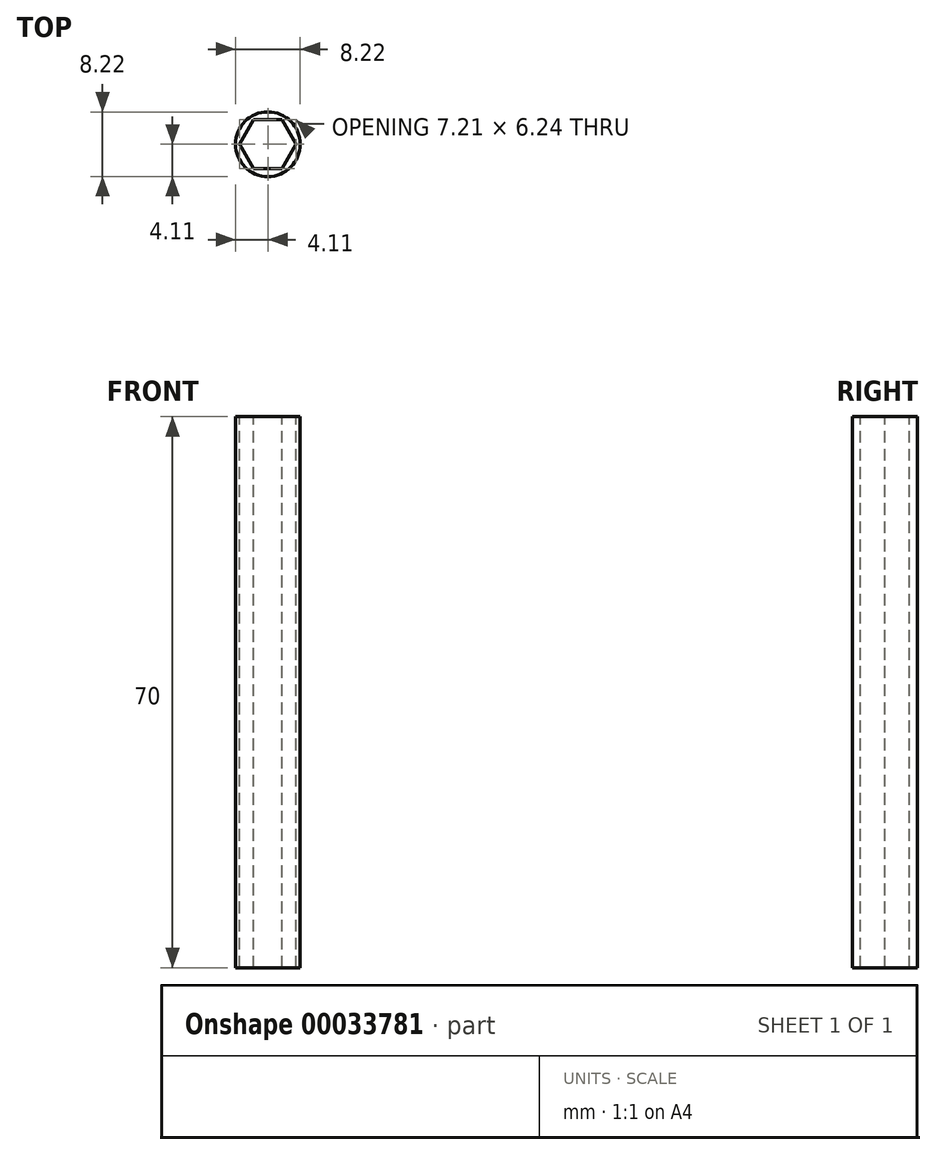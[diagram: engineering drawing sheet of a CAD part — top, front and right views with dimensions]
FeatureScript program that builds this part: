
annotation { "Feature Type Name" : "Feature", "Feature Type Description" : "" }
export const myFeature = defineFeature(function(context is Context, id is Id, definition is map)
    precondition{}
    {
        {
            var Q0;
            Q0=qCreatedBy(makeId("Top.planeOp"),FACE);
            var sketch = newSketch(context, id + "F0", { "sketchPlane" : qUnion([Q0])});
            skCircle(sketch, "E0", {"center": v(0, 0) * mm, "radius": 4.11 * mm});
            skSolve(sketch);
        }
        {
            var Q0;
            Q0=makeQuery(id+"F0.imprint","IMPRINT",FACE,{"disambiguationData":[TD([[makeQuery(id+"F0.imprint","IMPRINT",EDGE,{"derivedFrom":sQuery(id+"F0.wireOp",EDGE,"E0")}),1.0]])]});
            extrude(context, id + "F1", {"entities" : qUnion([Q0]), "depth" : 70 * mm});
        }
        {
            var Q0;
            Q0=makeQuery(id+"F1.opExtrude","CAP_FACE",FACE,{"disambiguationData":[OSD([sQuery(id+"F0.wireOp",EDGE,"E0")])],"isStart":false});
            var sketch = newSketch(context, id + "F2", { "sketchPlane" : qUnion([Q0])});
            skCircle(sketch, "E1.cCircle", {"center": v(0, 0) * mm, "radius": 3.12 * mm, "construction": true});
            skLineSegment(sketch, "E1.0", {"start": v(1.8, -3.12) * mm, "end": v(-1.8, -3.12) * mm});
            skLineSegment(sketch, "E1.1", {"start": v(-1.8, -3.12) * mm, "end": v(-3.6, 0) * mm});
            skLineSegment(sketch, "E1.2", {"start": v(-3.6, 0) * mm, "end": v(-1.8, 3.12) * mm});
            skLineSegment(sketch, "E1.3", {"start": v(-1.8, 3.12) * mm, "end": v(1.8, 3.12) * mm});
            skLineSegment(sketch, "E1.4", {"start": v(1.8, 3.12) * mm, "end": v(3.6, 0) * mm});
            skLineSegment(sketch, "E1.5", {"start": v(3.6, 0) * mm, "end": v(1.8, -3.12) * mm});
            skPoint(sketch, "E1.0.midPoint", {"position": v(0, -3.12) * mm});
            skSolve(sketch);
        }
        {
            var Q0;
            Q0=makeQuery(id+"F2.imprint","IMPRINT",FACE,{"disambiguationData":[TD([[makeQuery(id+"F2.imprint","IMPRINT",EDGE,{"derivedFrom":sQuery(id+"F2.wireOp",EDGE,"E1.0")}),-1.0]])]});
            extrude(context, id + "F3", {"entities" : qUnion([Q0]), "operationType" : NewBodyOperationType.REMOVE, "endBound" : BoundingType.THROUGH_ALL, "oppositeDirection" : true, "depth" : 25 * mm});
        }
    });
